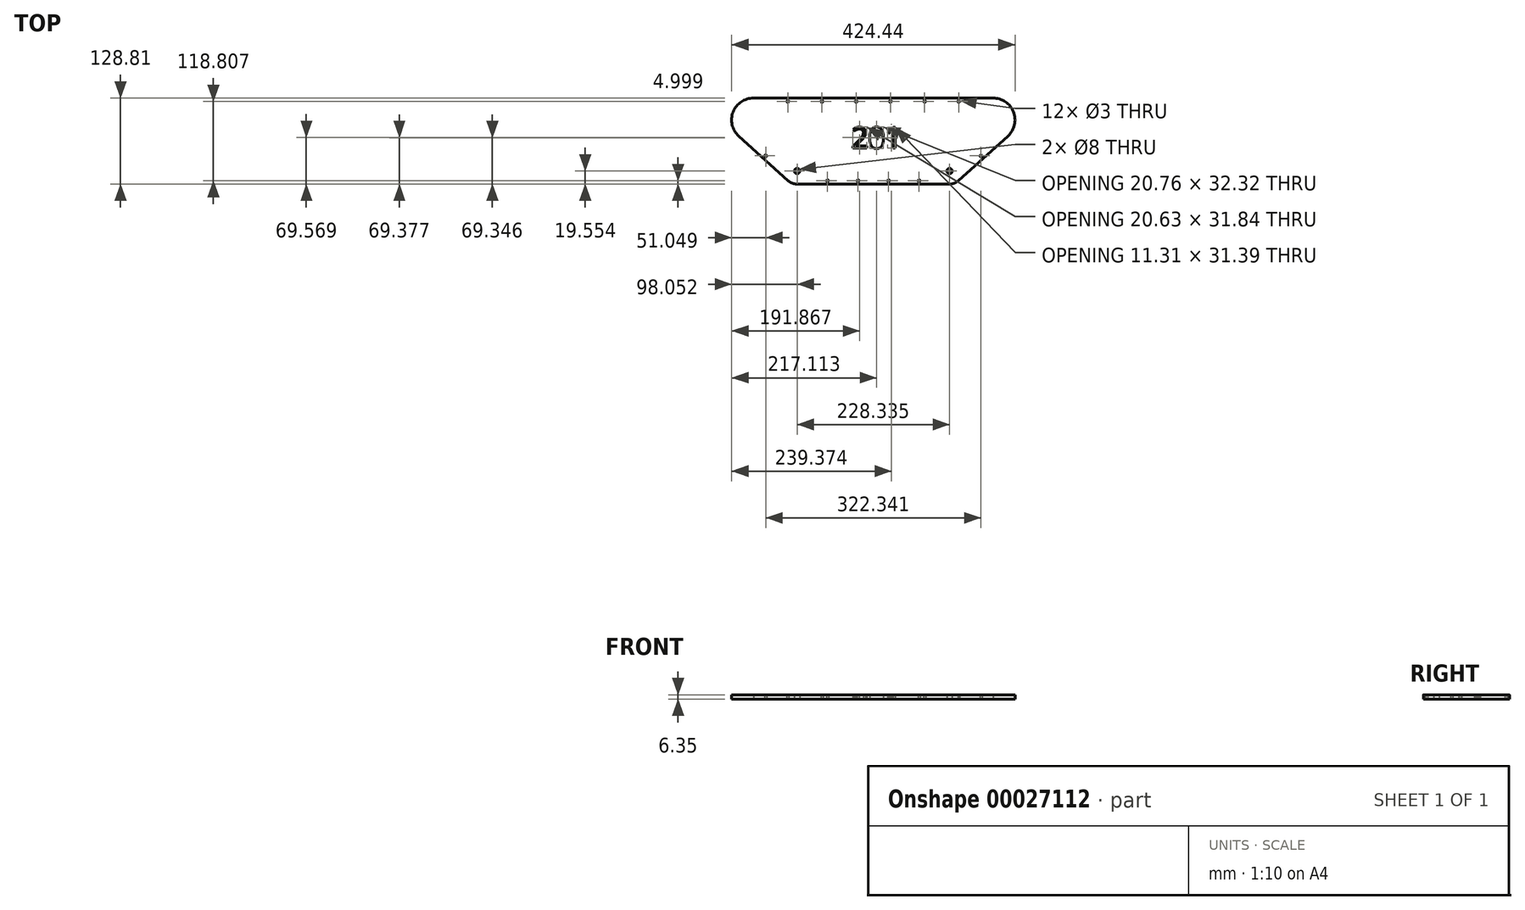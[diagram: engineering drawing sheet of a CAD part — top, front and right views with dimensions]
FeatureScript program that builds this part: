
annotation { "Feature Type Name" : "Feature", "Feature Type Description" : "" }
export const myFeature = defineFeature(function(context is Context, id is Id, definition is map)
    precondition{}
    {
        {
            var Q0;
            Q0=qCreatedBy(makeId("Top.planeOp"),FACE);
            var sketch = newSketch(context, id + "F0", { "sketchPlane" : qUnion([Q0])});
            skLineSegment(sketch, "E0", {"start": v(0, 100.1) * mm, "end": v(-179.26, 100.1) * mm});
            skLineSegment(sketch, "E1", {"start": v(0, 100.1) * mm, "end": v(0, -28.7) * mm});
            skCircle(sketch, "E2", {"center": v(-114.17, -9.15) * mm, "radius": 4 * mm});
            skLineSegment(sketch, "E3", {"start": v(-201.51, 43.34) * mm, "end": v(-127.55, -23.66) * mm});
            skLineSegment(sketch, "E4", {"start": v(0, -28.7) * mm, "end": v(-114.3, -28.7) * mm});
            skArc(sketch, "E5", {"start": v(-179.26, 100.1) * mm, "mid": v(-209.97, 79.4) * mm, "end": v(-201.51, 43.34) * mm});
            skLineSegment(sketch, "E6.MirrorCS", {"start": v(0, 100.1) * mm, "end": v(179.26, 100.1) * mm});
            skArc(sketch, "E7.MirrorCS", {"start": v(179.26, 100.1) * mm, "mid": v(209.97, 79.4) * mm, "end": v(201.51, 43.34) * mm});
            skLineSegment(sketch, "E8.MirrorCS", {"start": v(201.51, 43.34) * mm, "end": v(127.55, -23.66) * mm});
            skArc(sketch, "E9", {"start": v(-127.55, -23.66) * mm, "mid": v(-121.4, -27.42) * mm, "end": v(-114.3, -28.7) * mm});
            skArc(sketch, "E10.MirrorCS", {"start": v(127.55, -23.66) * mm, "mid": v(121.4, -27.42) * mm, "end": v(114.3, -28.7) * mm});
            skCircle(sketch, "E11.MirrorC", {"center": v(114.17, -9.15) * mm, "radius": 4 * mm});
            skLineSegment(sketch, "E12.MirrorCS", {"start": v(0, -28.7) * mm, "end": v(114.3, -28.7) * mm});
            skCircle(sketch, "E13", {"center": v(-68.58, -23.7) * mm, "radius": 1.5 * mm});
            skPoint(sketch, "E14", {"position": v(-68.58, -28.7) * mm});
            skPoint(sketch, "E15", {"position": v(-22.86, -28.7) * mm});
            skCircle(sketch, "E16", {"center": v(-22.86, -23.7) * mm, "radius": 1.5 * mm});
            skPoint(sketch, "E17", {"position": v(-128.05, 100.1) * mm});
            skPoint(sketch, "E18", {"position": v(-76.84, 100.1) * mm});
            skPoint(sketch, "E19", {"position": v(-25.64, 100.1) * mm});
            skCircle(sketch, "E20", {"center": v(-128.05, 95.1) * mm, "radius": 1.5 * mm});
            skCircle(sketch, "E21", {"center": v(-76.84, 95.1) * mm, "radius": 1.5 * mm});
            skCircle(sketch, "E22", {"center": v(-25.64, 95.1) * mm, "radius": 1.5 * mm});
            skCircle(sketch, "E23.MirrorC", {"center": v(68.58, -23.7) * mm, "radius": 1.5 * mm});
            skCircle(sketch, "E24.MirrorC", {"center": v(22.86, -23.7) * mm, "radius": 1.5 * mm});
            skCircle(sketch, "E25.MirrorC", {"center": v(128.05, 95.1) * mm, "radius": 1.5 * mm});
            skCircle(sketch, "E26.MirrorC", {"center": v(76.84, 95.1) * mm, "radius": 1.5 * mm});
            skCircle(sketch, "E27.MirrorC", {"center": v(25.64, 95.1) * mm, "radius": 1.5 * mm});
            skText(sketch, "E28", { "text": "201", "fontName": "OpenSans-Regular.ttf"});
            skPoint(sketch, "E29", {"position": v(111.07, 100.1) * mm});
            skCircle(sketch, "E30", {"center": v(-161.17, 13.55) * mm, "radius": 1.5 * mm});
            skCircle(sketch, "E31.MirrorC", {"center": v(161.17, 13.55) * mm, "radius": 1.5 * mm});
            const initialGuessF0  = {"E28": [-0.03282, 0.02495, 1, 0, 0.03166]};
            skSetInitialGuess(sketch, initialGuessF0);
            skSolve(sketch);
        }
        {
            var Q0;
            Q0=qSketchRegion(id+"F0",true);
            extrude(context, id + "F1", {"entities" : qUnion([Q0]), "depth" : 6.35 * mm});
        }
    });
